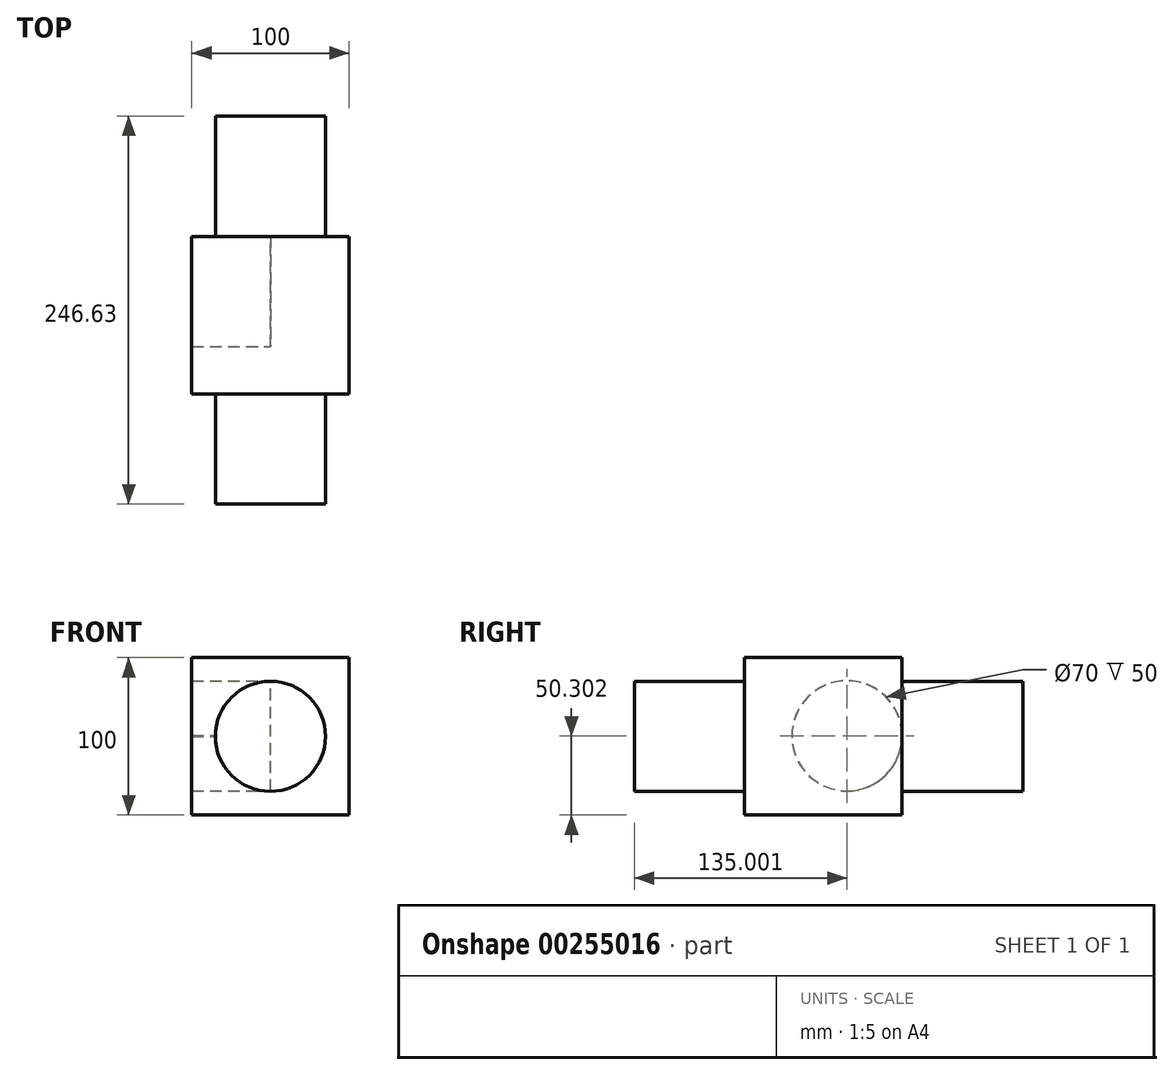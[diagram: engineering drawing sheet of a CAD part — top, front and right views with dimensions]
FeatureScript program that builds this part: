
annotation { "Feature Type Name" : "Feature", "Feature Type Description" : "" }
export const myFeature = defineFeature(function(context is Context, id is Id, definition is map)
    precondition{}
    {
        {
            var Q0;
            Q0=qCreatedBy(makeId("Front.planeOp"),FACE);
            var sketch = newSketch(context, id + "F0", { "sketchPlane" : qUnion([Q0])});
            skLineSegment(sketch, "E0.bottom", {"start": v(50, 50) * mm, "end": v(-50, 50) * mm});
            skLineSegment(sketch, "E0.top", {"start": v(50, -50) * mm, "end": v(-50, -50) * mm});
            skLineSegment(sketch, "E0.left", {"start": v(50, 50) * mm, "end": v(50, -50) * mm});
            skLineSegment(sketch, "E0.right", {"start": v(-50, 50) * mm, "end": v(-50, -50) * mm});
            skPoint(sketch, "E0.middle", {"position": v(0, 0) * mm});
            skSolve(sketch);
        }
        {
            var Q0;
            Q0 = qSketchRegion(id + "F0", true);
            extrude(context, id + "F1", {"entities" : qUnion([Q0]), "depth" : 100 * mm});
        }
        {
            var Q0;
            Q0=qCreatedBy(makeId("Front.planeOp"),FACE);
            var sketch = newSketch(context, id + "F2", { "sketchPlane" : qUnion([Q0])});
            skCircle(sketch, "E1", {"center": v(0, 0) * mm, "radius": 35 * mm});
            skSolve(sketch);
        }
        {
            var Q0;
            Q0 = qSketchRegion(id + "F2", true);
            extrude(context, id + "F3", {"entities" : qUnion([Q0]), "operationType" : NewBodyOperationType.ADD, "depth" : 170 * mm});
        }
        {
            var Q0;
            Q0=qCreatedBy(makeId("Front.planeOp"),FACE);
            var sketch = newSketch(context, id + "F4", { "sketchPlane" : qUnion([Q0])});
            skCircle(sketch, "E2", {"center": v(0, 0) * mm, "radius": 35 * mm});
            skSolve(sketch);
        }
        {
            var Q0;
            Q0 = qSketchRegion(id + "F4", true);
            extrude(context, id + "F5", {"entities" : qUnion([Q0]), "operationType" : NewBodyOperationType.ADD, "depth" : 161.96 * mm, "hasSecondDirection" : true, "secondDirectionOppositeDirection" : true, "secondDirectionDepth" : 76.63 * mm});
        }
        {
            var Q0;
            Q0=qCreatedBy(makeId("Right.planeOp"),FACE);
            var sketch = newSketch(context, id + "F6", { "sketchPlane" : qUnion([Q0])});
            skCircle(sketch, "E3", {"center": v(-35, 0.3) * mm, "radius": 35 * mm});
            skPoint(sketch, "E3.first.point", {"position": v(0, 0) * mm});
            skPoint(sketch, "E3.second.point", {"position": v(-70, 0) * mm});
            skPoint(sketch, "E3.third.point", {"position": v(-14.97, 29) * mm});
            skSolve(sketch);
        }
        {
            var Q0;
            Q0 = qSketchRegion(id + "F6", true);
            extrude(context, id + "F7", {"entities" : qUnion([Q0]), "operationType" : NewBodyOperationType.REMOVE, "oppositeDirection" : true, "depth" : 1320.8 * mm});
        }
    });
